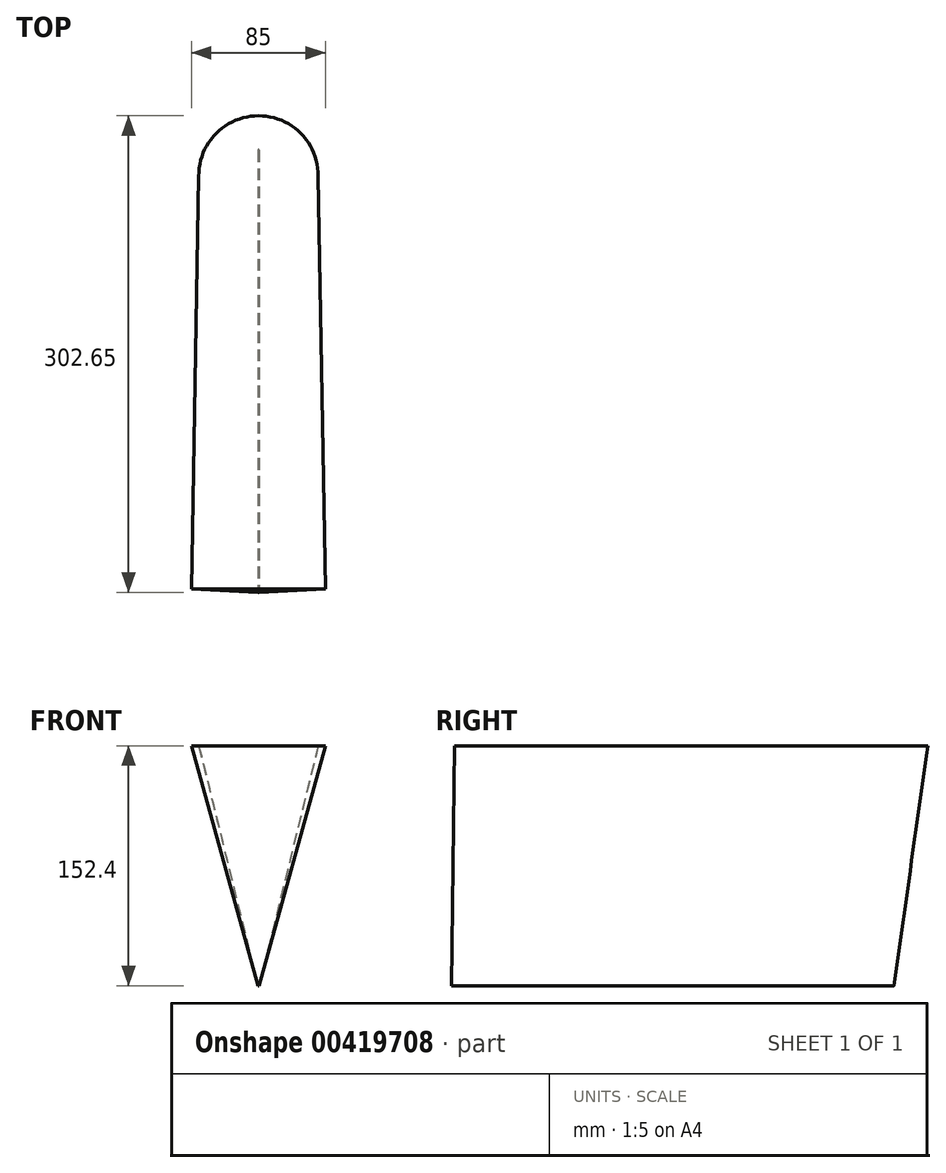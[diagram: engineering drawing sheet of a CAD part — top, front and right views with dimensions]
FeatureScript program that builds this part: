
annotation { "Feature Type Name" : "Feature", "Feature Type Description" : "" }
export const myFeature = defineFeature(function(context is Context, id is Id, definition is map)
    precondition{}
    {
        {
            var Q0;
            Q0=qCreatedBy(makeId("Top.planeOp"),FACE);
            cPlane(context, id + "F0", {"entities" : qUnion([Q0]), "cplaneType" : CPlaneType.OFFSET, "offset" : 152.4 * mm, "width" : 152.4 * mm, "height" : 152.4 * mm});
        }
        {
            var Q0;
            Q0=qCreatedBy(id+"F0.planeOp",FACE);
            var sketch = newSketch(context, id + "F1", { "sketchPlane" : qUnion([Q0])});
            skLineSegment(sketch, "E0", {"start": v(42.5, -194) * mm, "end": v(37.93, 68.3) * mm});
            skLineSegment(sketch, "E1", {"start": v(-42.5, -194) * mm, "end": v(-37.93, 68.3) * mm});
            skLineSegment(sketch, "E2", {"start": v(-42.5, -194) * mm, "end": v(42.5, -194) * mm});
            skArc(sketch, "E3", {"start": v(37.93, 68.3) * mm, "mid": v(0, 106.5) * mm, "end": v(-37.93, 68.3) * mm});
            skSolve(sketch);
        }
        {
            var Q0;
            Q0=qCreatedBy(makeId("Top.planeOp"),FACE);
            var sketch = newSketch(context, id + "F2", { "sketchPlane" : qUnion([Q0])});
            skLineSegment(sketch, "E4", {"start": v(-0.38, -196.14) * mm, "end": v(0.38, -196.14) * mm});
            skArc(sketch, "E5", {"start": v(0.38, 84.6) * mm, "mid": v(0, 84.98) * mm, "end": v(-0.38, 84.6) * mm});
            skLineSegment(sketch, "E6", {"start": v(-0.38, 84.6) * mm, "end": v(-0.38, -196.14) * mm});
            skLineSegment(sketch, "E7", {"start": v(0.38, 84.6) * mm, "end": v(0.38, -196.14) * mm});
            skSolve(sketch);
        }
        {
            var Q0;
            Q0 = qSketchRegion(id + "F1", true);
            var Q1;
            Q1 = qSketchRegion(id + "F2", true);
            loft(context, id + "F3", {"sheetProfilesArray" : [{ "sheetProfileEntities" : qUnion([Q0]) }, { "sheetProfileEntities" : qUnion([Q1]) }]});
        }
    });
